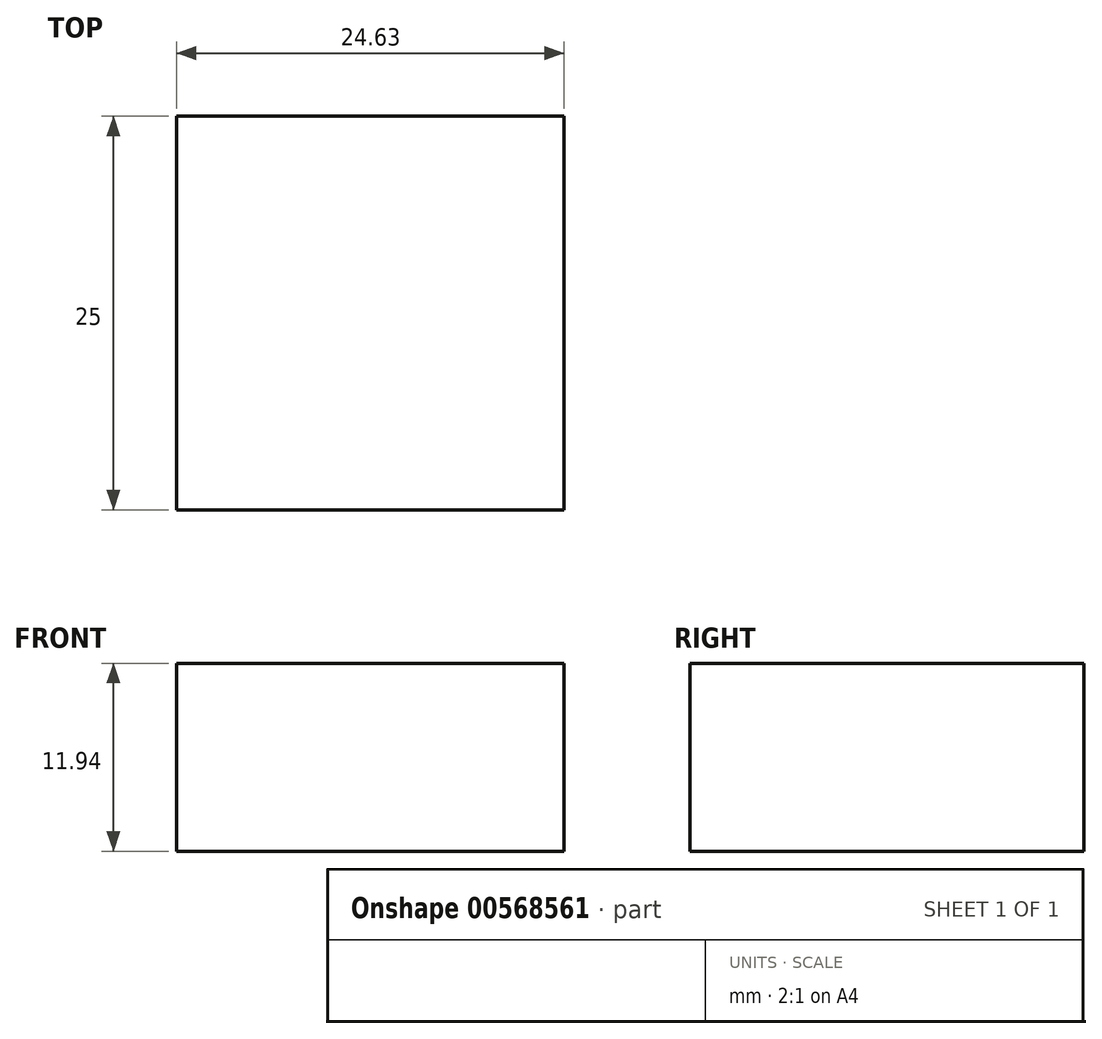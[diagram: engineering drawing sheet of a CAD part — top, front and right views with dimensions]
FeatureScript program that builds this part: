
annotation { "Feature Type Name" : "Feature", "Feature Type Description" : "" }
export const myFeature = defineFeature(function(context is Context, id is Id, definition is map)
    precondition{}
    {
        {
            var Q0;
            Q0=qCreatedBy(makeId("Front.planeOp"),FACE);
            var sketch = newSketch(context, id + "F0", { "sketchPlane" : qUnion([Q0])});
            skLineSegment(sketch, "E0.bottom", {"start": v(-75.21, 0) * mm, "end": v(-50.58, 0) * mm});
            skLineSegment(sketch, "E0.top", {"start": v(-75.21, 11.94) * mm, "end": v(-50.58, 11.94) * mm});
            skLineSegment(sketch, "E0.left", {"start": v(-75.21, 0) * mm, "end": v(-75.21, 11.94) * mm});
            skLineSegment(sketch, "E0.right", {"start": v(-50.58, 0) * mm, "end": v(-50.58, 11.94) * mm});
            skLineSegment(sketch, "E1.bottom", {"start": v(-75.21, 0) * mm, "end": v(-36.58, 0) * mm});
            skLineSegment(sketch, "E1.top", {"start": v(-75.21, 18.29) * mm, "end": v(-36.58, 18.29) * mm});
            skLineSegment(sketch, "E1.left", {"start": v(-75.21, 0) * mm, "end": v(-75.21, 18.29) * mm});
            skLineSegment(sketch, "E1.right", {"start": v(-36.58, 0) * mm, "end": v(-36.58, 18.29) * mm});
            skSolve(sketch);
        }
        {
            var Q0;
            {var subQ0=sQuery(id+"F0.wireOp",EDGE,"E0.top");Q0=makeQuery(id+"F0.imprint","IMPRINT",FACE,{"disambiguationData":[TD([[makeQuery(id+"F0.imprint","IMPRINT",EDGE,{"derivedFrom":subQ0}),-1.0]])]});}
            extrude(context, id + "F1", {"entities" : qUnion([Q0]), "depth" : 25 * mm, "offsetDistance" : 25 * mm});
        }
    });
